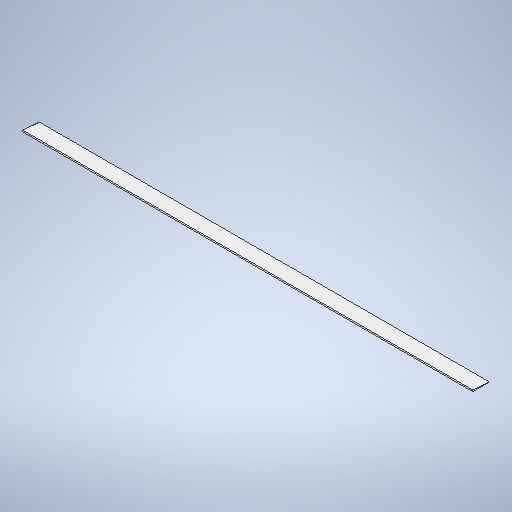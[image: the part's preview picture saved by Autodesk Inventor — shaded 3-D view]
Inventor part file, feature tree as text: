
AUTODESK INVENTOR PART (.ipt)
format: ipt  version: 2025.1 (Build 291241020, 241B)  size: 250,880 bytes
history: native  units: in
note: dims shown in document units (in); Inventor stores cm internally (conversion verified against a paired STEP export)
features: extrude x1, sketch x1
ambient origin geometry x8: Origin, YZ Plane, XZ Plane, XY Plane, X Axis, Y Axis, Z Axis, Center Point
bodies: Solid1 (feature_tree)
feature tree (2):
  extrude  "Extrusion1"  Depth=1.0in
  sketch  "Sketch1"  dims[d0=11.0in d1=1.0in d2=294.825in d3=0.0in]
